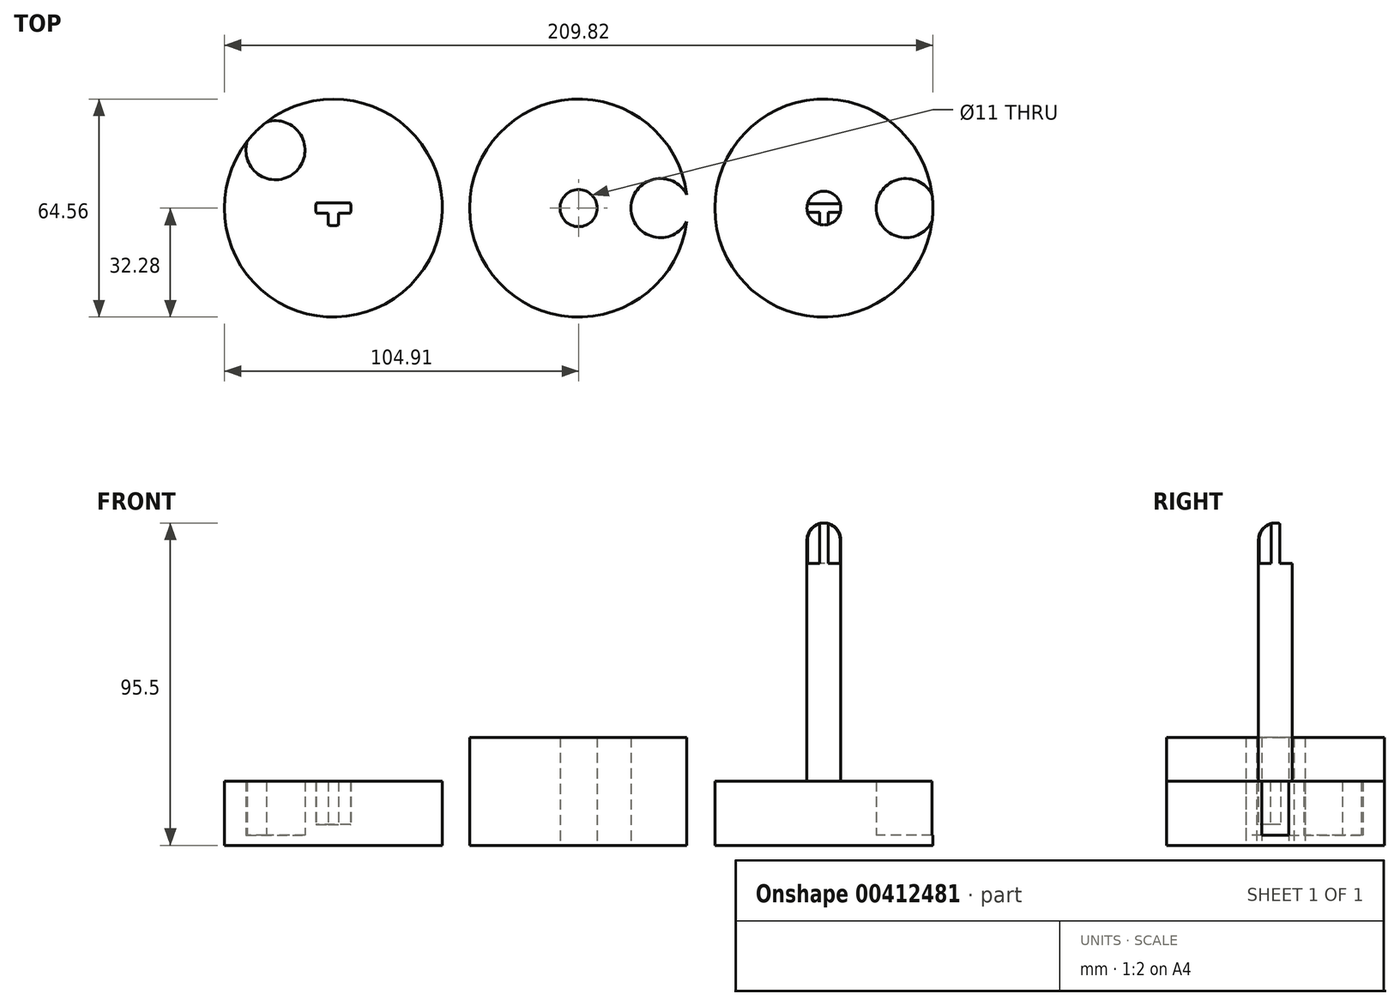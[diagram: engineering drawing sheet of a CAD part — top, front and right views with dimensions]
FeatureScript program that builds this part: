
annotation { "Feature Type Name" : "Feature", "Feature Type Description" : "" }
export const myFeature = defineFeature(function(context is Context, id is Id, definition is map)
    precondition{}
    {
        {
            assignVariable(context, id + "F0", {"name" : "MarbleDiameterMM", "anyValue" : 16});
        }
        {
            assignVariable(context, id + "F1", {"name" : "AxisDiameterMM", "anyValue" : 10});
        }
        {
            assignVariable(context, id + "F2", {"name" : "LidStrengthMM", "anyValue" : 3});
        }
        {
            var Q0;
            Q0=qCreatedBy(makeId("Top.planeOp"),FACE);
            var sketch = newSketch(context, id + "F3", { "sketchPlane" : qUnion([Q0])});
            skCircle(sketch, "E0", {"center": v(0, 0) * mm, "radius": 5.5 * mm});
            skArc(sketch, "E1", {"start": v(32.03, 4) * mm, "mid": v(15.5, 0) * mm, "end": v(32.03, -4) * mm});
            skCircle(sketch, "E2", {"center": v(0, 0) * mm, "radius": 32.28 * mm});
            skPoint(sketch, "E3", {"position": v(72.63, 0) * mm});
            skCircle(sketch, "E4", {"center": v(72.63, 0) * mm, "radius": 5 * mm});
            skCircle(sketch, "E5", {"center": v(72.63, 0) * mm, "radius": 32.28 * mm});
            skLineSegment(sketch, "E6", {"start": v(72.63, 0) * mm, "end": v(96.88, 0) * mm, "construction": true});
            skArc(sketch, "E7", {"start": v(104.66, 4) * mm, "mid": v(88.13, 0) * mm, "end": v(104.66, -4) * mm});
            skLineSegment(sketch, "E8", {"start": v(72.63, 0) * mm, "end": v(72.63, -16.43) * mm, "construction": true});
            skLineSegment(sketch, "E9.MirrorCS", {"start": v(67.8, -1.25) * mm, "end": v(71.38, -1.25) * mm});
            skLineSegment(sketch, "E10.trimOffspring", {"start": v(71.38, -1.25) * mm, "end": v(71.38, -4.84) * mm});
            skLineSegment(sketch, "E11.trimOffspring", {"start": v(73.88, -1.25) * mm, "end": v(77.47, -1.25) * mm});
            skLineSegment(sketch, "E12.trimOffspring", {"start": v(73.88, -1.25) * mm, "end": v(73.88, -4.84) * mm});
            skLineSegment(sketch, "E13", {"start": v(0, 0) * mm, "end": v(-72.63, 0) * mm, "construction": true});
            skCircle(sketch, "E14", {"center": v(-72.63, 0) * mm, "radius": 32.28 * mm});
            skLineSegment(sketch, "E15", {"start": v(-72.63, 0) * mm, "end": v(-89.78, 17.15) * mm, "construction": true});
            skArc(sketch, "E16", {"start": v(-98.11, 19.82) * mm, "mid": v(-83.6, 10.96) * mm, "end": v(-92.45, 25.48) * mm});
            skLineSegment(sketch, "E17", {"start": v(-67.6, 1.5) * mm, "end": v(-71.13, 1.5) * mm});
            skLineSegment(sketch, "E18.MirrorCS", {"start": v(-71.13, -1.5) * mm, "end": v(-71.13, -5.03) * mm});
            skLineSegment(sketch, "E19.MirrorCS", {"start": v(-67.6, -1.5) * mm, "end": v(-71.13, -1.5) * mm});
            skLineSegment(sketch, "E20", {"start": v(-72.63, 14.24) * mm, "end": v(-72.63, -17.77) * mm, "construction": true});
            skLineSegment(sketch, "E21.MirrorCS", {"start": v(-77.66, 1.5) * mm, "end": v(-74.13, 1.5) * mm});
            skLineSegment(sketch, "E22.MirrorCS", {"start": v(-77.66, -1.5) * mm, "end": v(-74.13, -1.5) * mm});
            skLineSegment(sketch, "E23.MirrorCS", {"start": v(-74.13, -1.5) * mm, "end": v(-74.13, -5.03) * mm});
            skArc(sketch, "E24.trimOffspring", {"start": v(-77.66, 1.5) * mm, "mid": v(-77.88, 0) * mm, "end": v(-77.66, -1.5) * mm});
            skArc(sketch, "E25.trimOffspring", {"start": v(-74.13, -5.03) * mm, "mid": v(-72.63, -5.25) * mm, "end": v(-71.13, -5.03) * mm});
            skArc(sketch, "E26.trimOffspring", {"start": v(-67.6, -1.5) * mm, "mid": v(-67.38, 0) * mm, "end": v(-67.6, 1.5) * mm});
            skLineSegment(sketch, "E27", {"start": v(-71.13, 1.5) * mm, "end": v(-74.13, 1.5) * mm});
            skPoint(sketch, "E28.trimOffspring.end.orphan", {"position": v(77.47, 1.25) * mm});
            skPoint(sketch, "E29.start.orphan", {"position": v(67.8, 1.25) * mm});
            skLineSegment(sketch, "E30", {"start": v(77.47, 1.25) * mm, "end": v(67.8, 1.25) * mm});
            skSolve(sketch);
        }
        {
            var Q0;
            Q0=qCreatedBy(makeId("Right.planeOp"),FACE);
            var sketch = newSketch(context, id + "F4", { "sketchPlane" : qUnion([Q0])});
            skLineSegment(sketch, "E31", {"start": v(0, -53.7) * mm, "end": v(0, 51.4) * mm, "construction": true});
            skSolve(sketch);
        }
        {
            var Q0;
            Q0=qCreatedBy(makeId("Front.planeOp"),FACE);
            var sketch = newSketch(context, id + "F5", { "sketchPlane" : qUnion([Q0])});
            skLineSegment(sketch, "E32", {"start": v(72.63, 0) * mm, "end": v(72.63, 48.98) * mm, "construction": true});
            skSolve(sketch);
        }
        {
            var Q0;
            Q0=makeQuery(id+"F3.imprint","IMPRINT",FACE,{"disambiguationData":[TD([[makeQuery(id+"F3.imprint","IMPRINT",EDGE,{"derivedFrom":sQuery(id+"F3.wireOp",EDGE,"E0")}),-1.0]])]});
            var Q1;
            {var subQ0=sQuery(id+"F3.wireOp",EDGE,"E1");Q1=makeQuery(id+"F3.imprint","IMPRINT",FACE,{"disambiguationData":[TD([[makeQuery(id+"F3.imprint","IMPRINT",EDGE,{"derivedFrom":subQ0}),1.0]])]});}
            extrude(context, id + "F6", {"entities" : qUnion([Q0, Q1]), "depth" : (getVariable(context, 'MarbleDiameterMM') * 2) * mm});
        }
        {
            var Q0;
            {var subQ0=sQuery(id+"F3.wireOp",EDGE,"E1");Q0=makeQuery(id+"F3.imprint","IMPRINT",FACE,{"disambiguationData":[TD([[makeQuery(id+"F3.imprint","IMPRINT",EDGE,{"derivedFrom":subQ0}),1.0]])]});}
            extrude(context, id + "F7", {"entities" : qUnion([Q0]), "operationType" : NewBodyOperationType.REMOVE, "endBound" : BoundingType.THROUGH_ALL, "depth" : 25 * mm});
        }
        {
            var Q0;
            {var subQ9=sQuery(id+"F3.wireOp",EDGE,"E7");Q0=makeQuery(id+"F3.imprint","IMPRINT",FACE,{"disambiguationData":[TD([[makeQuery(id+"F3.imprint","IMPRINT",EDGE,{"derivedFrom":subQ9}),-1.0]])]});}
            var Q1;
            {var subQ0=sQuery(id+"F3.wireOp",EDGE,"E11.trimOffspring");Q1=makeQuery(id+"F3.imprint","IMPRINT",FACE,{"disambiguationData":[TD([[makeQuery(id+"F3.imprint","IMPRINT",EDGE,{"derivedFrom":subQ0}),-1.0]])]});}
            var Q2;
            {var subQ2=sQuery(id+"F3.wireOp",EDGE,"ZirwGm3F-62kP-VicB-J87Z-jw9RzvwtjYrb");Q2=makeQuery(id+"F3.imprint","IMPRINT",FACE,{"disambiguationData":[TD([[makeQuery(id+"F3.imprint","IMPRINT",EDGE,{"derivedFrom":subQ2}),1.0]])]});}
            var Q3;
            {var subQ0=sQuery(id+"F3.wireOp",EDGE,"E9.MirrorCS");Q3=makeQuery(id+"F3.imprint","IMPRINT",FACE,{"disambiguationData":[TD([[makeQuery(id+"F3.imprint","IMPRINT",EDGE,{"derivedFrom":subQ0}),-1.0]])]});}
            var Q4;
            {var subQ0=sQuery(id+"F3.wireOp",EDGE,"ZirwGm3F-62kP-VicB-J87Z-jw9RzvwtjYrb");Q4=makeQuery(id+"F3.imprint","IMPRINT",FACE,{"disambiguationData":[TD([[makeQuery(id+"F3.imprint","IMPRINT",EDGE,{"derivedFrom":subQ0}),-1.0]])]});}
            var Q5;
            {var subQ0=sQuery(id+"F3.wireOp",EDGE,"919ad380-31ac-4220-b41f-6fd3feb1b4c40.MirrorCS");Q5=makeQuery(id+"F3.imprint","IMPRINT",FACE,{"disambiguationData":[TD([[makeQuery(id+"F3.imprint","IMPRINT",EDGE,{"derivedFrom":subQ0}),1.0]])]});}
            var Q6;
            {var subQ0=sQuery(id+"F3.wireOp",EDGE,"E7");Q6=makeQuery(id+"F3.imprint","IMPRINT",FACE,{"disambiguationData":[TD([[makeQuery(id+"F3.imprint","IMPRINT",EDGE,{"derivedFrom":subQ0}),1.0]])]});}
            extrude(context, id + "F8", {"entities" : qUnion([Q0, Q1, Q2, Q3, Q4, Q5, Q6]), "depth" : (getVariable(context, 'LidStrengthMM') + getVariable(context, 'MarbleDiameterMM')) * mm});
        }
        {
            var Q0;
            {var subQ0=sQuery(id+"F3.wireOp",EDGE,"E9.MirrorCS");Q0=makeQuery(id+"F3.imprint","IMPRINT",FACE,{"disambiguationData":[TD([[makeQuery(id+"F3.imprint","IMPRINT",EDGE,{"derivedFrom":subQ0}),1.0]])]});}
            extrude(context, id + "F9", {"entities" : qUnion([Q0]), "operationType" : NewBodyOperationType.ADD, "depth" : (getVariable(context, 'LidStrengthMM') + 5.75 * getVariable(context, 'MarbleDiameterMM') + .5) * mm});
        }
        {
            var Q0;
            {var subQ0=sQuery(id+"F3.wireOp",EDGE,"ZirwGm3F-62kP-VicB-J87Z-jw9RzvwtjYrb");Q0=makeQuery(id+"F3.imprint","IMPRINT",FACE,{"disambiguationData":[TD([[makeQuery(id+"F3.imprint","IMPRINT",EDGE,{"derivedFrom":subQ0}),-1.0]])]});}
            var Q1;
            {var subQ0=sQuery(id+"F3.wireOp",EDGE,"E9.MirrorCS");Q1=makeQuery(id+"F3.imprint","IMPRINT",FACE,{"disambiguationData":[TD([[makeQuery(id+"F3.imprint","IMPRINT",EDGE,{"derivedFrom":subQ0}),-1.0]])]});}
            var Q2;
            {var subQ0=sQuery(id+"F3.wireOp",EDGE,"E11.trimOffspring");Q2=makeQuery(id+"F3.imprint","IMPRINT",FACE,{"disambiguationData":[TD([[makeQuery(id+"F3.imprint","IMPRINT",EDGE,{"derivedFrom":subQ0}),-1.0]])]});}
            var Q3;
            {var subQ0=sQuery(id+"F3.wireOp",EDGE,"919ad380-31ac-4220-b41f-6fd3feb1b4c40.MirrorCS");Q3=makeQuery(id+"F3.imprint","IMPRINT",FACE,{"disambiguationData":[TD([[makeQuery(id+"F3.imprint","IMPRINT",EDGE,{"derivedFrom":subQ0}),1.0]])]});}
            var Q4;
            {var subQ0=sQuery(id+"F3.wireOp",EDGE,"E30");Q4=makeQuery(id+"F3.imprint","IMPRINT",FACE,{"disambiguationData":[TD([[makeQuery(id+"F3.imprint","IMPRINT",EDGE,{"derivedFrom":subQ0}),-1.0]])]});}
            extrude(context, id + "F10", {"entities" : qUnion([Q0, Q1, Q2, Q3, Q4]), "operationType" : NewBodyOperationType.ADD, "depth" : (5 * getVariable(context, 'MarbleDiameterMM') + getVariable(context, 'LidStrengthMM') + .5) * mm});
        }
        {
            var Q0;
            {var subQ0=sQuery(id+"F3.wireOp",EDGE,"E4");Q0=makeQuery(id+"F9.opExtrude","CAP_EDGE",EDGE,{"disambiguationData":[OSD([subQ0]),TDD([makeQuery(id+"F3.imprint","IMPRINT",EDGE,{"disambiguationData":[TD([[makeQuery(id+"F3.imprint","INTERSECT",VERTEX,{"derivedFrom":[subQ0,sQuery(id+"F3.wireOp",EDGE,"E10.trimOffspring")]}),-1.0]])],"derivedFrom":subQ0})])],"isStart":false});}
            fillet(context, id + "F11", {"entities" : qUnion([Q0]), "radius" : (getVariable(context, 'AxisDiameterMM') / 2) * mm, "tangentPropagation" : true, "allowEdgeOverflow" : false});
        }
        {
            var Q0;
            {var subQ0=sQuery(id+"F3.wireOp",EDGE,"E7");Q0=makeQuery(id+"F3.imprint","IMPRINT",FACE,{"disambiguationData":[TD([[makeQuery(id+"F3.imprint","IMPRINT",EDGE,{"derivedFrom":subQ0}),1.0]])]});}
            var Q1;
            Q1=sQuery(id+"F3.wireOp",EDGE,"E7");
            extrude(context, id + "F12", {"entities" : qUnion([Q0]), "operationType" : NewBodyOperationType.REMOVE, "surfaceEntities" : qUnion([Q1]), "endBound" : BoundingType.THROUGH_ALL, "depth" : 25 * mm, "hasSecondDirection" : true, "secondDirectionOppositeDirection" : false, "secondDirectionDepth" : (getVariable(context, 'LidStrengthMM')) * mm});
        }
        {
            var Q0;
            {var subQ0=sQuery(id+"F3.wireOp",EDGE,"E7");Q0=makeQuery(id+"F3.imprint","IMPRINT",FACE,{"disambiguationData":[TD([[makeQuery(id+"F3.imprint","IMPRINT",EDGE,{"derivedFrom":subQ0}),1.0]])]});}
            extrude(context, id + "F13", {"entities" : qUnion([Q0]), "operationType" : NewBodyOperationType.REMOVE, "endBound" : BoundingType.THROUGH_ALL, "depth" : 20.6 * mm, "hasSecondDirection" : true, "secondDirectionOppositeDirection" : false, "secondDirectionDepth" : getVariable(context, 'LidStrengthMM') * mm});
        }
        {
            var Q0;
            {var subQ0=sQuery(id+"F3.wireOp",EDGE,"E16");Q0=makeQuery(id+"F3.imprint","IMPRINT",FACE,{"disambiguationData":[TD([[makeQuery(id+"F3.imprint","IMPRINT",EDGE,{"derivedFrom":subQ0}),-1.0]])]});}
            extrude(context, id + "F14", {"entities" : qUnion([Q0]), "depth" : (getVariable(context, 'LidStrengthMM') + getVariable(context, 'MarbleDiameterMM')) * mm});
        }
        {
            var Q0;
            Q0=makeQuery(id+"F3.imprint","IMPRINT",FACE,{"disambiguationData":[TD([[makeQuery(id+"F3.imprint","IMPRINT",EDGE,{"derivedFrom":sQuery(id+"F3.wireOp",EDGE,"E17")}),1.0]])]});
            extrude(context, id + "F15", {"entities" : qUnion([Q0]), "operationType" : NewBodyOperationType.ADD, "depth" : (getVariable(context, 'LidStrengthMM') + .2 * getVariable(context, 'MarbleDiameterMM')) * mm});
        }
        {
            var Q0;
            {var subQ0=sQuery(id+"F3.wireOp",EDGE,"E16");Q0=makeQuery(id+"F3.imprint","IMPRINT",FACE,{"disambiguationData":[TD([[makeQuery(id+"F3.imprint","IMPRINT",EDGE,{"derivedFrom":subQ0}),1.0]])]});}
            extrude(context, id + "F16", {"entities" : qUnion([Q0]), "operationType" : NewBodyOperationType.ADD, "depth" : (getVariable(context, 'LidStrengthMM')) * mm});
        }
    });
